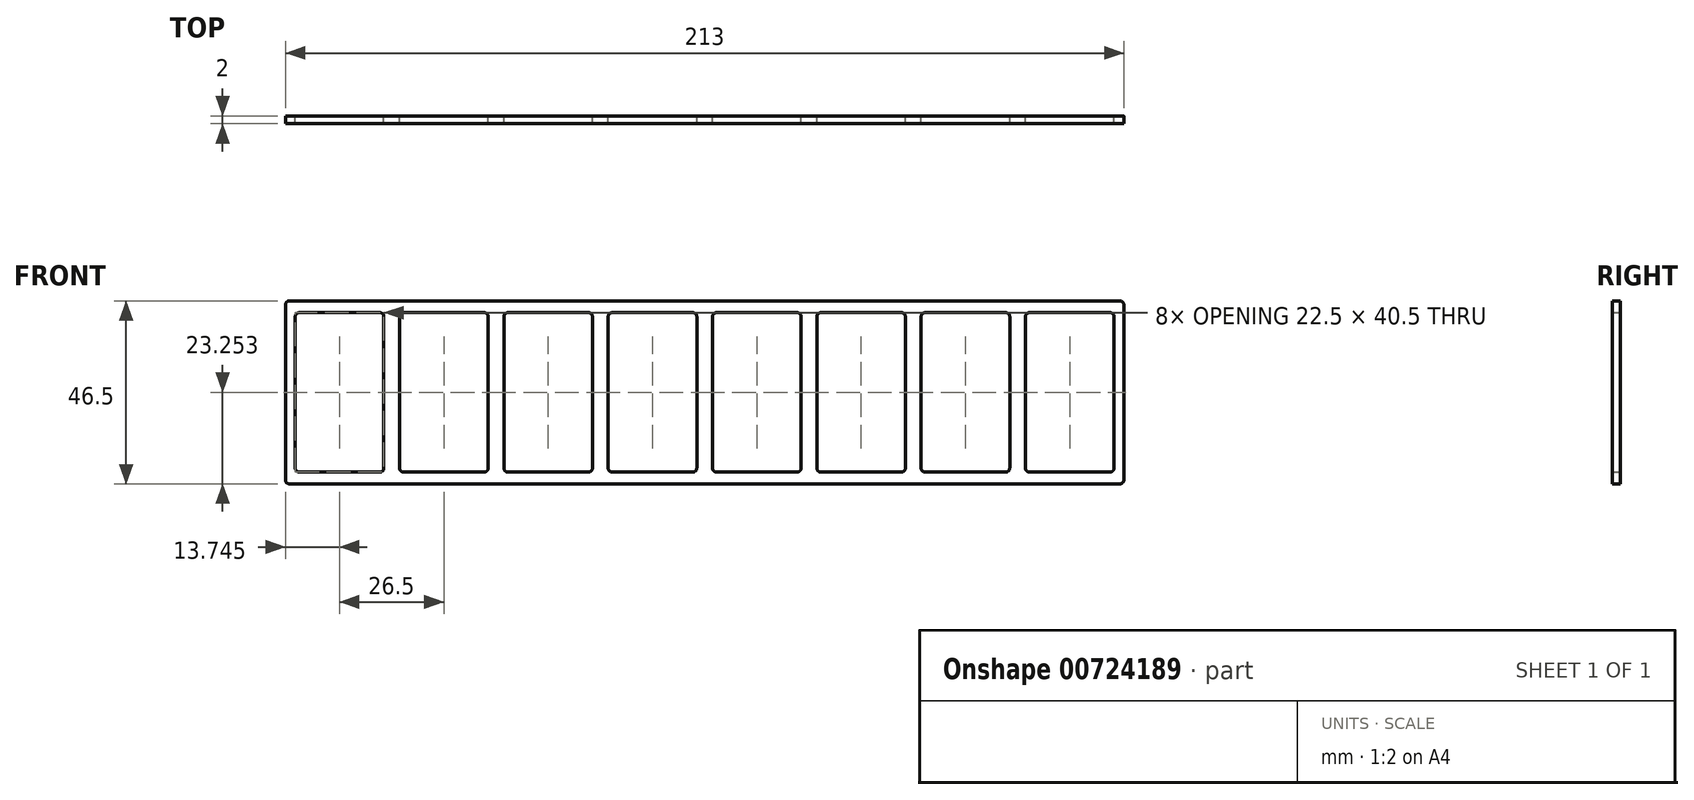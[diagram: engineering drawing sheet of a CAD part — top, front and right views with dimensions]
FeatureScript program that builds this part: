
annotation { "Feature Type Name" : "Feature", "Feature Type Description" : "" }
export const myFeature = defineFeature(function(context is Context, id is Id, definition is map)
    precondition{}
    {
        {
            var Q0;
            Q0=qCreatedBy(makeId("Front.planeOp"),FACE);
            var sketch = newSketch(context, id + "F0", { "sketchPlane" : qUnion([Q0])});
            skLineSegment(sketch, "E0.bottom", {"start": v(-105.08, 28.38) * mm, "end": v(107.92, 28.38) * mm});
            skLineSegment(sketch, "E0.top", {"start": v(-105.08, -18.12) * mm, "end": v(107.92, -18.12) * mm});
            skLineSegment(sketch, "E0.left", {"start": v(-105.08, 28.38) * mm, "end": v(-105.08, -18.12) * mm});
            skLineSegment(sketch, "E0.right", {"start": v(107.92, 28.38) * mm, "end": v(107.92, -18.12) * mm});
            skLineSegment(sketch, "E1.bottom", {"start": v(-102.58, 25.38) * mm, "end": v(-80.08, 25.38) * mm});
            skLineSegment(sketch, "E1.top", {"start": v(-102.58, -15.12) * mm, "end": v(-80.08, -15.12) * mm});
            skLineSegment(sketch, "E1.left", {"start": v(-102.58, 25.38) * mm, "end": v(-102.58, -15.12) * mm});
            skLineSegment(sketch, "E1.right", {"start": v(-80.08, 25.38) * mm, "end": v(-80.08, -15.12) * mm});
            skLineSegment(sketch, "E2.1.0.0", {"start": v(-76.08, 25.38) * mm, "end": v(-53.58, 25.38) * mm});
            skLineSegment(sketch, "E2.1.0.1", {"start": v(-53.58, 25.38) * mm, "end": v(-53.58, -15.12) * mm});
            skLineSegment(sketch, "E2.1.0.2", {"start": v(-76.08, -15.12) * mm, "end": v(-53.58, -15.12) * mm});
            skLineSegment(sketch, "E2.1.0.3", {"start": v(-76.08, 25.38) * mm, "end": v(-76.08, -15.12) * mm});
            skLineSegment(sketch, "E2.2.0.0", {"start": v(-49.58, 25.38) * mm, "end": v(-27.08, 25.38) * mm});
            skLineSegment(sketch, "E2.2.0.1", {"start": v(-27.08, 25.38) * mm, "end": v(-27.08, -15.12) * mm});
            skLineSegment(sketch, "E2.2.0.2", {"start": v(-49.58, -15.12) * mm, "end": v(-27.08, -15.12) * mm});
            skLineSegment(sketch, "E2.2.0.3", {"start": v(-49.58, 25.38) * mm, "end": v(-49.58, -15.12) * mm});
            skLineSegment(sketch, "E2.3.0.0", {"start": v(-23.08, 25.38) * mm, "end": v(-0.58, 25.38) * mm});
            skLineSegment(sketch, "E2.3.0.1", {"start": v(-0.58, 25.38) * mm, "end": v(-0.58, -15.12) * mm});
            skLineSegment(sketch, "E2.3.0.2", {"start": v(-23.08, -15.12) * mm, "end": v(-0.58, -15.12) * mm});
            skLineSegment(sketch, "E2.3.0.3", {"start": v(-23.08, 25.38) * mm, "end": v(-23.08, -15.12) * mm});
            skLineSegment(sketch, "E2.4.0.0", {"start": v(3.42, 25.38) * mm, "end": v(25.92, 25.38) * mm});
            skLineSegment(sketch, "E2.4.0.1", {"start": v(25.92, 25.38) * mm, "end": v(25.92, -15.12) * mm});
            skLineSegment(sketch, "E2.4.0.2", {"start": v(3.42, -15.12) * mm, "end": v(25.92, -15.12) * mm});
            skLineSegment(sketch, "E2.4.0.3", {"start": v(3.42, 25.38) * mm, "end": v(3.42, -15.12) * mm});
            skLineSegment(sketch, "E2.5.0.0", {"start": v(29.92, 25.38) * mm, "end": v(52.42, 25.38) * mm});
            skLineSegment(sketch, "E2.5.0.1", {"start": v(52.42, 25.38) * mm, "end": v(52.42, -15.12) * mm});
            skLineSegment(sketch, "E2.5.0.2", {"start": v(29.92, -15.12) * mm, "end": v(52.42, -15.12) * mm});
            skLineSegment(sketch, "E2.5.0.3", {"start": v(29.92, 25.38) * mm, "end": v(29.92, -15.12) * mm});
            skLineSegment(sketch, "E2.6.0.0", {"start": v(56.42, 25.38) * mm, "end": v(78.92, 25.38) * mm});
            skLineSegment(sketch, "E2.6.0.1", {"start": v(78.92, 25.38) * mm, "end": v(78.92, -15.12) * mm});
            skLineSegment(sketch, "E2.6.0.2", {"start": v(56.42, -15.12) * mm, "end": v(78.92, -15.12) * mm});
            skLineSegment(sketch, "E2.6.0.3", {"start": v(56.42, 25.38) * mm, "end": v(56.42, -15.12) * mm});
            skLineSegment(sketch, "E2.7.0.0", {"start": v(82.92, 25.38) * mm, "end": v(105.42, 25.38) * mm});
            skLineSegment(sketch, "E2.7.0.1", {"start": v(105.42, 25.38) * mm, "end": v(105.42, -15.12) * mm});
            skLineSegment(sketch, "E2.7.0.2", {"start": v(82.92, -15.12) * mm, "end": v(105.42, -15.12) * mm});
            skLineSegment(sketch, "E2.7.0.3", {"start": v(82.92, 25.38) * mm, "end": v(82.92, -15.12) * mm});
            skLineSegment(sketch, "E2.direction1", {"start": v(-102.58, 25.38) * mm, "end": v(-76.08, 25.38) * mm, "construction": true});
            skSolve(sketch);
        }
        {
            var Q0;
            Q0=makeQuery(id+"F0.imprint","IMPRINT",FACE,{"disambiguationData":[TD([[makeQuery(id+"F0.imprint","IMPRINT",EDGE,{"derivedFrom":sQuery(id+"F0.wireOp",EDGE,"E0.bottom")}),-1.0]])]});
            extrude(context, id + "F1", {"entities" : qUnion([Q0]), "depth" : 2 * mm, "offsetDistance" : 25 * mm});
        }
        {
            var Q0;
            Q0=makeQuery(id+"F1.opExtrude","SWEPT_EDGE",EDGE,{"disambiguationData":[OSD([sQuery(id+"F0.wireOp",EDGE,"E1.bottom"),sQuery(id+"F0.wireOp",EDGE,"E1.right")])]});
            var Q1;
            Q1=makeQuery(id+"F1.opExtrude","SWEPT_EDGE",EDGE,{"disambiguationData":[OSD([sQuery(id+"F0.wireOp",EDGE,"E1.bottom"),sQuery(id+"F0.wireOp",EDGE,"E1.left")])]});
            var Q2;
            Q2=makeQuery(id+"F1.opExtrude","SWEPT_EDGE",EDGE,{"disambiguationData":[OSD([sQuery(id+"F0.wireOp",EDGE,"E1.top"),sQuery(id+"F0.wireOp",EDGE,"E1.right")])]});
            var Q3;
            Q3=makeQuery(id+"F1.opExtrude","SWEPT_EDGE",EDGE,{"disambiguationData":[OSD([sQuery(id+"F0.wireOp",EDGE,"E1.top"),sQuery(id+"F0.wireOp",EDGE,"E1.left")])]});
            var Q4;
            Q4=makeQuery(id+"F1.opExtrude","SWEPT_EDGE",EDGE,{"disambiguationData":[OSD([sQuery(id+"F0.wireOp",EDGE,"e407004c-ae19-40fa-b78e-cd4ba2a1ce8c.1.0.0"),sQuery(id+"F0.wireOp",EDGE,"e407004c-ae19-40fa-b78e-cd4ba2a1ce8c.1.0.3")])]});
            var Q5;
            Q5=makeQuery(id+"F1.opExtrude","SWEPT_EDGE",EDGE,{"disambiguationData":[OSD([sQuery(id+"F0.wireOp",EDGE,"e407004c-ae19-40fa-b78e-cd4ba2a1ce8c.1.0.0"),sQuery(id+"F0.wireOp",EDGE,"e407004c-ae19-40fa-b78e-cd4ba2a1ce8c.1.0.1")])]});
            var Q6;
            Q6=makeQuery(id+"F1.opExtrude","SWEPT_EDGE",EDGE,{"disambiguationData":[OSD([sQuery(id+"F0.wireOp",EDGE,"e407004c-ae19-40fa-b78e-cd4ba2a1ce8c.2.0.0"),sQuery(id+"F0.wireOp",EDGE,"e407004c-ae19-40fa-b78e-cd4ba2a1ce8c.2.0.1")])]});
            var Q7;
            Q7=makeQuery(id+"F1.opExtrude","SWEPT_EDGE",EDGE,{"disambiguationData":[OSD([sQuery(id+"F0.wireOp",EDGE,"915b7015-1165-4992-a895-0c7eab26e4c1.0.3.0"),sQuery(id+"F0.wireOp",EDGE,"915b7015-1165-4992-a895-0c7eab26e4c1.3.3.0")])]});
            var Q8;
            Q8=makeQuery(id+"F1.opExtrude","SWEPT_EDGE",EDGE,{"disambiguationData":[OSD([sQuery(id+"F0.wireOp",EDGE,"e407004c-ae19-40fa-b78e-cd4ba2a1ce8c.2.0.0"),sQuery(id+"F0.wireOp",EDGE,"e407004c-ae19-40fa-b78e-cd4ba2a1ce8c.2.0.3")])]});
            var Q9;
            Q9=makeQuery(id+"F1.opExtrude","SWEPT_EDGE",EDGE,{"disambiguationData":[OSD([sQuery(id+"F0.wireOp",EDGE,"e407004c-ae19-40fa-b78e-cd4ba2a1ce8c.1.0.2"),sQuery(id+"F0.wireOp",EDGE,"e407004c-ae19-40fa-b78e-cd4ba2a1ce8c.1.0.3")])]});
            var Q10;
            Q10=makeQuery(id+"F1.opExtrude","SWEPT_EDGE",EDGE,{"disambiguationData":[OSD([sQuery(id+"F0.wireOp",EDGE,"e407004c-ae19-40fa-b78e-cd4ba2a1ce8c.1.0.1"),sQuery(id+"F0.wireOp",EDGE,"e407004c-ae19-40fa-b78e-cd4ba2a1ce8c.1.0.2")])]});
            var Q11;
            Q11=makeQuery(id+"F1.opExtrude","SWEPT_EDGE",EDGE,{"disambiguationData":[OSD([sQuery(id+"F0.wireOp",EDGE,"e407004c-ae19-40fa-b78e-cd4ba2a1ce8c.2.0.1"),sQuery(id+"F0.wireOp",EDGE,"e407004c-ae19-40fa-b78e-cd4ba2a1ce8c.2.0.2")])]});
            var Q12;
            Q12=makeQuery(id+"F1.opExtrude","SWEPT_EDGE",EDGE,{"disambiguationData":[OSD([sQuery(id+"F0.wireOp",EDGE,"915b7015-1165-4992-a895-0c7eab26e4c1.0.3.0"),sQuery(id+"F0.wireOp",EDGE,"915b7015-1165-4992-a895-0c7eab26e4c1.9.3.0")])]});
            var Q13;
            Q13=makeQuery(id+"F1.opExtrude","SWEPT_EDGE",EDGE,{"disambiguationData":[OSD([sQuery(id+"F0.wireOp",EDGE,"915b7015-1165-4992-a895-0c7eab26e4c1.6.3.0"),sQuery(id+"F0.wireOp",EDGE,"915b7015-1165-4992-a895-0c7eab26e4c1.9.3.0")])]});
            var Q14;
            Q14=makeQuery(id+"F1.opExtrude","SWEPT_EDGE",EDGE,{"disambiguationData":[OSD([sQuery(id+"F0.wireOp",EDGE,"915b7015-1165-4992-a895-0c7eab26e4c1.3.3.0"),sQuery(id+"F0.wireOp",EDGE,"915b7015-1165-4992-a895-0c7eab26e4c1.6.3.0")])]});
            var Q15;
            Q15=makeQuery(id+"F1.opExtrude","SWEPT_EDGE",EDGE,{"disambiguationData":[OSD([sQuery(id+"F0.wireOp",EDGE,"915b7015-1165-4992-a895-0c7eab26e4c1.6.4.0"),sQuery(id+"F0.wireOp",EDGE,"915b7015-1165-4992-a895-0c7eab26e4c1.9.4.0")])]});
            var Q16;
            Q16=makeQuery(id+"F1.opExtrude","SWEPT_EDGE",EDGE,{"disambiguationData":[OSD([sQuery(id+"F0.wireOp",EDGE,"915b7015-1165-4992-a895-0c7eab26e4c1.0.4.0"),sQuery(id+"F0.wireOp",EDGE,"915b7015-1165-4992-a895-0c7eab26e4c1.9.4.0")])]});
            var Q17;
            Q17=makeQuery(id+"F1.opExtrude","SWEPT_EDGE",EDGE,{"disambiguationData":[OSD([sQuery(id+"F0.wireOp",EDGE,"915b7015-1165-4992-a895-0c7eab26e4c1.0.4.0"),sQuery(id+"F0.wireOp",EDGE,"915b7015-1165-4992-a895-0c7eab26e4c1.3.4.0")])]});
            var Q18;
            Q18=makeQuery(id+"F1.opExtrude","SWEPT_EDGE",EDGE,{"disambiguationData":[OSD([sQuery(id+"F0.wireOp",EDGE,"915b7015-1165-4992-a895-0c7eab26e4c1.0.5.0"),sQuery(id+"F0.wireOp",EDGE,"915b7015-1165-4992-a895-0c7eab26e4c1.3.5.0")])]});
            var Q19;
            Q19=makeQuery(id+"F1.opExtrude","SWEPT_EDGE",EDGE,{"disambiguationData":[OSD([sQuery(id+"F0.wireOp",EDGE,"915b7015-1165-4992-a895-0c7eab26e4c1.0.6.0"),sQuery(id+"F0.wireOp",EDGE,"915b7015-1165-4992-a895-0c7eab26e4c1.3.6.0")])]});
            var Q20;
            Q20=makeQuery(id+"F1.opExtrude","SWEPT_EDGE",EDGE,{"disambiguationData":[OSD([sQuery(id+"F0.wireOp",EDGE,"915b7015-1165-4992-a895-0c7eab26e4c1.0.5.0"),sQuery(id+"F0.wireOp",EDGE,"915b7015-1165-4992-a895-0c7eab26e4c1.9.5.0")])]});
            var Q21;
            Q21=makeQuery(id+"F1.opExtrude","SWEPT_EDGE",EDGE,{"disambiguationData":[OSD([sQuery(id+"F0.wireOp",EDGE,"915b7015-1165-4992-a895-0c7eab26e4c1.0.6.0"),sQuery(id+"F0.wireOp",EDGE,"915b7015-1165-4992-a895-0c7eab26e4c1.9.6.0")])]});
            var Q22;
            Q22=makeQuery(id+"F1.opExtrude","SWEPT_EDGE",EDGE,{"disambiguationData":[OSD([sQuery(id+"F0.wireOp",EDGE,"915b7015-1165-4992-a895-0c7eab26e4c1.3.4.0"),sQuery(id+"F0.wireOp",EDGE,"915b7015-1165-4992-a895-0c7eab26e4c1.6.4.0")])]});
            var Q23;
            Q23=makeQuery(id+"F1.opExtrude","SWEPT_EDGE",EDGE,{"disambiguationData":[OSD([sQuery(id+"F0.wireOp",EDGE,"915b7015-1165-4992-a895-0c7eab26e4c1.3.5.0"),sQuery(id+"F0.wireOp",EDGE,"915b7015-1165-4992-a895-0c7eab26e4c1.6.5.0")])]});
            var Q24;
            Q24=makeQuery(id+"F1.opExtrude","SWEPT_EDGE",EDGE,{"disambiguationData":[OSD([sQuery(id+"F0.wireOp",EDGE,"915b7015-1165-4992-a895-0c7eab26e4c1.3.6.0"),sQuery(id+"F0.wireOp",EDGE,"915b7015-1165-4992-a895-0c7eab26e4c1.6.6.0")])]});
            var Q25;
            Q25=makeQuery(id+"F1.opExtrude","SWEPT_EDGE",EDGE,{"disambiguationData":[OSD([sQuery(id+"F0.wireOp",EDGE,"915b7015-1165-4992-a895-0c7eab26e4c1.6.6.0"),sQuery(id+"F0.wireOp",EDGE,"915b7015-1165-4992-a895-0c7eab26e4c1.9.6.0")])]});
            var Q26;
            Q26=makeQuery(id+"F1.opExtrude","SWEPT_EDGE",EDGE,{"disambiguationData":[OSD([sQuery(id+"F0.wireOp",EDGE,"915b7015-1165-4992-a895-0c7eab26e4c1.6.5.0"),sQuery(id+"F0.wireOp",EDGE,"915b7015-1165-4992-a895-0c7eab26e4c1.9.5.0")])]});
            var Q27;
            Q27=makeQuery(id+"F1.opExtrude","SWEPT_EDGE",EDGE,{"disambiguationData":[OSD([sQuery(id+"F0.wireOp",EDGE,"e407004c-ae19-40fa-b78e-cd4ba2a1ce8c.2.0.2"),sQuery(id+"F0.wireOp",EDGE,"e407004c-ae19-40fa-b78e-cd4ba2a1ce8c.2.0.3")])]});
            var Q28;
            Q28=makeQuery(id+"F1.opExtrude","SWEPT_EDGE",EDGE,{"disambiguationData":[OSD([sQuery(id+"F0.wireOp",EDGE,"E0.bottom"),sQuery(id+"F0.wireOp",EDGE,"E0.right")])]});
            var Q29;
            Q29=makeQuery(id+"F1.opExtrude","SWEPT_EDGE",EDGE,{"disambiguationData":[OSD([sQuery(id+"F0.wireOp",EDGE,"E0.top"),sQuery(id+"F0.wireOp",EDGE,"E0.right")])]});
            var Q30;
            Q30=makeQuery(id+"F1.opExtrude","SWEPT_EDGE",EDGE,{"disambiguationData":[OSD([sQuery(id+"F0.wireOp",EDGE,"E0.bottom"),sQuery(id+"F0.wireOp",EDGE,"E0.left")])]});
            var Q31;
            Q31=makeQuery(id+"F1.opExtrude","SWEPT_EDGE",EDGE,{"disambiguationData":[OSD([sQuery(id+"F0.wireOp",EDGE,"E0.top"),sQuery(id+"F0.wireOp",EDGE,"E0.left")])]});
            var Q32;
            Q32=makeQuery(id+"F1.opExtrude","SWEPT_EDGE",EDGE,{"disambiguationData":[OSD([sQuery(id+"F0.wireOp",EDGE,"92b8a9f3-a869-450a-bc62-c86c763e5b85.6.7.0"),sQuery(id+"F0.wireOp",EDGE,"92b8a9f3-a869-450a-bc62-c86c763e5b85.9.7.0")])]});
            var Q33;
            Q33=makeQuery(id+"F1.opExtrude","SWEPT_EDGE",EDGE,{"disambiguationData":[OSD([sQuery(id+"F0.wireOp",EDGE,"92b8a9f3-a869-450a-bc62-c86c763e5b85.0.7.0"),sQuery(id+"F0.wireOp",EDGE,"92b8a9f3-a869-450a-bc62-c86c763e5b85.9.7.0")])]});
            var Q34;
            Q34=makeQuery(id+"F1.opExtrude","SWEPT_EDGE",EDGE,{"disambiguationData":[OSD([sQuery(id+"F0.wireOp",EDGE,"92b8a9f3-a869-450a-bc62-c86c763e5b85.0.7.0"),sQuery(id+"F0.wireOp",EDGE,"92b8a9f3-a869-450a-bc62-c86c763e5b85.3.7.0")])]});
            var Q35;
            Q35=makeQuery(id+"F1.opExtrude","SWEPT_EDGE",EDGE,{"disambiguationData":[OSD([sQuery(id+"F0.wireOp",EDGE,"92b8a9f3-a869-450a-bc62-c86c763e5b85.3.7.0"),sQuery(id+"F0.wireOp",EDGE,"92b8a9f3-a869-450a-bc62-c86c763e5b85.6.7.0")])]});
            var Q36;
            Q36=makeQuery(id+"F1.opExtrude","SWEPT_EDGE",EDGE,{"disambiguationData":[OSD([sQuery(id+"F0.wireOp",EDGE,"E2.1.0.0"),sQuery(id+"F0.wireOp",EDGE,"E2.1.0.3")])]});
            var Q37;
            Q37=makeQuery(id+"F1.opExtrude","SWEPT_EDGE",EDGE,{"disambiguationData":[OSD([sQuery(id+"F0.wireOp",EDGE,"E2.2.0.0"),sQuery(id+"F0.wireOp",EDGE,"E2.2.0.3")])]});
            var Q38;
            Q38=makeQuery(id+"F1.opExtrude","SWEPT_EDGE",EDGE,{"disambiguationData":[OSD([sQuery(id+"F0.wireOp",EDGE,"E2.3.0.0"),sQuery(id+"F0.wireOp",EDGE,"E2.3.0.3")])]});
            var Q39;
            Q39=makeQuery(id+"F1.opExtrude","SWEPT_EDGE",EDGE,{"disambiguationData":[OSD([sQuery(id+"F0.wireOp",EDGE,"E2.4.0.0"),sQuery(id+"F0.wireOp",EDGE,"E2.4.0.3")])]});
            var Q40;
            Q40=makeQuery(id+"F1.opExtrude","SWEPT_EDGE",EDGE,{"disambiguationData":[OSD([sQuery(id+"F0.wireOp",EDGE,"E2.5.0.0"),sQuery(id+"F0.wireOp",EDGE,"E2.5.0.3")])]});
            var Q41;
            Q41=makeQuery(id+"F1.opExtrude","SWEPT_EDGE",EDGE,{"disambiguationData":[OSD([sQuery(id+"F0.wireOp",EDGE,"E2.6.0.0"),sQuery(id+"F0.wireOp",EDGE,"E2.6.0.3")])]});
            var Q42;
            Q42=makeQuery(id+"F1.opExtrude","SWEPT_EDGE",EDGE,{"disambiguationData":[OSD([sQuery(id+"F0.wireOp",EDGE,"E2.7.0.0"),sQuery(id+"F0.wireOp",EDGE,"E2.7.0.3")])]});
            var Q43;
            Q43=makeQuery(id+"F1.opExtrude","SWEPT_EDGE",EDGE,{"disambiguationData":[OSD([sQuery(id+"F0.wireOp",EDGE,"E2.1.0.0"),sQuery(id+"F0.wireOp",EDGE,"E2.1.0.1")])]});
            var Q44;
            Q44=makeQuery(id+"F1.opExtrude","SWEPT_EDGE",EDGE,{"disambiguationData":[OSD([sQuery(id+"F0.wireOp",EDGE,"E2.2.0.0"),sQuery(id+"F0.wireOp",EDGE,"E2.2.0.1")])]});
            var Q45;
            Q45=makeQuery(id+"F1.opExtrude","SWEPT_EDGE",EDGE,{"disambiguationData":[OSD([sQuery(id+"F0.wireOp",EDGE,"E2.3.0.0"),sQuery(id+"F0.wireOp",EDGE,"E2.3.0.1")])]});
            var Q46;
            Q46=makeQuery(id+"F1.opExtrude","SWEPT_EDGE",EDGE,{"disambiguationData":[OSD([sQuery(id+"F0.wireOp",EDGE,"E2.4.0.0"),sQuery(id+"F0.wireOp",EDGE,"E2.4.0.1")])]});
            var Q47;
            Q47=makeQuery(id+"F1.opExtrude","SWEPT_EDGE",EDGE,{"disambiguationData":[OSD([sQuery(id+"F0.wireOp",EDGE,"E2.5.0.0"),sQuery(id+"F0.wireOp",EDGE,"E2.5.0.1")])]});
            var Q48;
            Q48=makeQuery(id+"F1.opExtrude","SWEPT_EDGE",EDGE,{"disambiguationData":[OSD([sQuery(id+"F0.wireOp",EDGE,"E2.6.0.0"),sQuery(id+"F0.wireOp",EDGE,"E2.6.0.1")])]});
            var Q49;
            Q49=makeQuery(id+"F1.opExtrude","SWEPT_EDGE",EDGE,{"disambiguationData":[OSD([sQuery(id+"F0.wireOp",EDGE,"E2.7.0.0"),sQuery(id+"F0.wireOp",EDGE,"E2.7.0.1")])]});
            var Q50;
            Q50=makeQuery(id+"F1.opExtrude","SWEPT_EDGE",EDGE,{"disambiguationData":[OSD([sQuery(id+"F0.wireOp",EDGE,"E2.1.0.2"),sQuery(id+"F0.wireOp",EDGE,"E2.1.0.3")])]});
            var Q51;
            Q51=makeQuery(id+"F1.opExtrude","SWEPT_EDGE",EDGE,{"disambiguationData":[OSD([sQuery(id+"F0.wireOp",EDGE,"E2.2.0.2"),sQuery(id+"F0.wireOp",EDGE,"E2.2.0.3")])]});
            var Q52;
            Q52=makeQuery(id+"F1.opExtrude","SWEPT_EDGE",EDGE,{"disambiguationData":[OSD([sQuery(id+"F0.wireOp",EDGE,"E2.3.0.2"),sQuery(id+"F0.wireOp",EDGE,"E2.3.0.3")])]});
            var Q53;
            Q53=makeQuery(id+"F1.opExtrude","SWEPT_EDGE",EDGE,{"disambiguationData":[OSD([sQuery(id+"F0.wireOp",EDGE,"E2.4.0.2"),sQuery(id+"F0.wireOp",EDGE,"E2.4.0.3")])]});
            var Q54;
            Q54=makeQuery(id+"F1.opExtrude","SWEPT_EDGE",EDGE,{"disambiguationData":[OSD([sQuery(id+"F0.wireOp",EDGE,"E2.5.0.2"),sQuery(id+"F0.wireOp",EDGE,"E2.5.0.3")])]});
            var Q55;
            Q55=makeQuery(id+"F1.opExtrude","SWEPT_EDGE",EDGE,{"disambiguationData":[OSD([sQuery(id+"F0.wireOp",EDGE,"E2.6.0.2"),sQuery(id+"F0.wireOp",EDGE,"E2.6.0.3")])]});
            var Q56;
            Q56=makeQuery(id+"F1.opExtrude","SWEPT_EDGE",EDGE,{"disambiguationData":[OSD([sQuery(id+"F0.wireOp",EDGE,"E2.7.0.2"),sQuery(id+"F0.wireOp",EDGE,"E2.7.0.3")])]});
            var Q57;
            Q57=makeQuery(id+"F1.opExtrude","SWEPT_EDGE",EDGE,{"disambiguationData":[OSD([sQuery(id+"F0.wireOp",EDGE,"E2.1.0.1"),sQuery(id+"F0.wireOp",EDGE,"E2.1.0.2")])]});
            var Q58;
            Q58=makeQuery(id+"F1.opExtrude","SWEPT_EDGE",EDGE,{"disambiguationData":[OSD([sQuery(id+"F0.wireOp",EDGE,"E2.2.0.1"),sQuery(id+"F0.wireOp",EDGE,"E2.2.0.2")])]});
            var Q59;
            Q59=makeQuery(id+"F1.opExtrude","SWEPT_EDGE",EDGE,{"disambiguationData":[OSD([sQuery(id+"F0.wireOp",EDGE,"E2.3.0.1"),sQuery(id+"F0.wireOp",EDGE,"E2.3.0.2")])]});
            var Q60;
            Q60=makeQuery(id+"F1.opExtrude","SWEPT_EDGE",EDGE,{"disambiguationData":[OSD([sQuery(id+"F0.wireOp",EDGE,"E2.4.0.1"),sQuery(id+"F0.wireOp",EDGE,"E2.4.0.2")])]});
            var Q61;
            Q61=makeQuery(id+"F1.opExtrude","SWEPT_EDGE",EDGE,{"disambiguationData":[OSD([sQuery(id+"F0.wireOp",EDGE,"E2.5.0.1"),sQuery(id+"F0.wireOp",EDGE,"E2.5.0.2")])]});
            var Q62;
            Q62=makeQuery(id+"F1.opExtrude","SWEPT_EDGE",EDGE,{"disambiguationData":[OSD([sQuery(id+"F0.wireOp",EDGE,"E2.6.0.1"),sQuery(id+"F0.wireOp",EDGE,"E2.6.0.2")])]});
            var Q63;
            Q63=makeQuery(id+"F1.opExtrude","SWEPT_EDGE",EDGE,{"disambiguationData":[OSD([sQuery(id+"F0.wireOp",EDGE,"E2.7.0.1"),sQuery(id+"F0.wireOp",EDGE,"E2.7.0.2")])]});
            fillet(context, id + "F2", {"entities" : qUnion([Q0, Q1, Q2, Q3, Q4, Q5, Q6, Q7, Q8, Q9, Q10, Q11, Q12, Q13, Q14, Q15, Q16, Q17, Q18, Q19, Q20, Q21, Q22, Q23, Q24, Q25, Q26, Q27, Q28, Q29, Q30, Q31, Q32, Q33, Q34, Q35, Q36, Q37, Q38, Q39, Q40, Q41, Q42, Q43, Q44, Q45, Q46, Q47, Q48, Q49, Q50, Q51, Q52, Q53, Q54, Q55, Q56, Q57, Q58, Q59, Q60, Q61, Q62, Q63]), "radius" : 1 * mm, "tangentPropagation" : true, "allowEdgeOverflow" : false});
        }
    });
